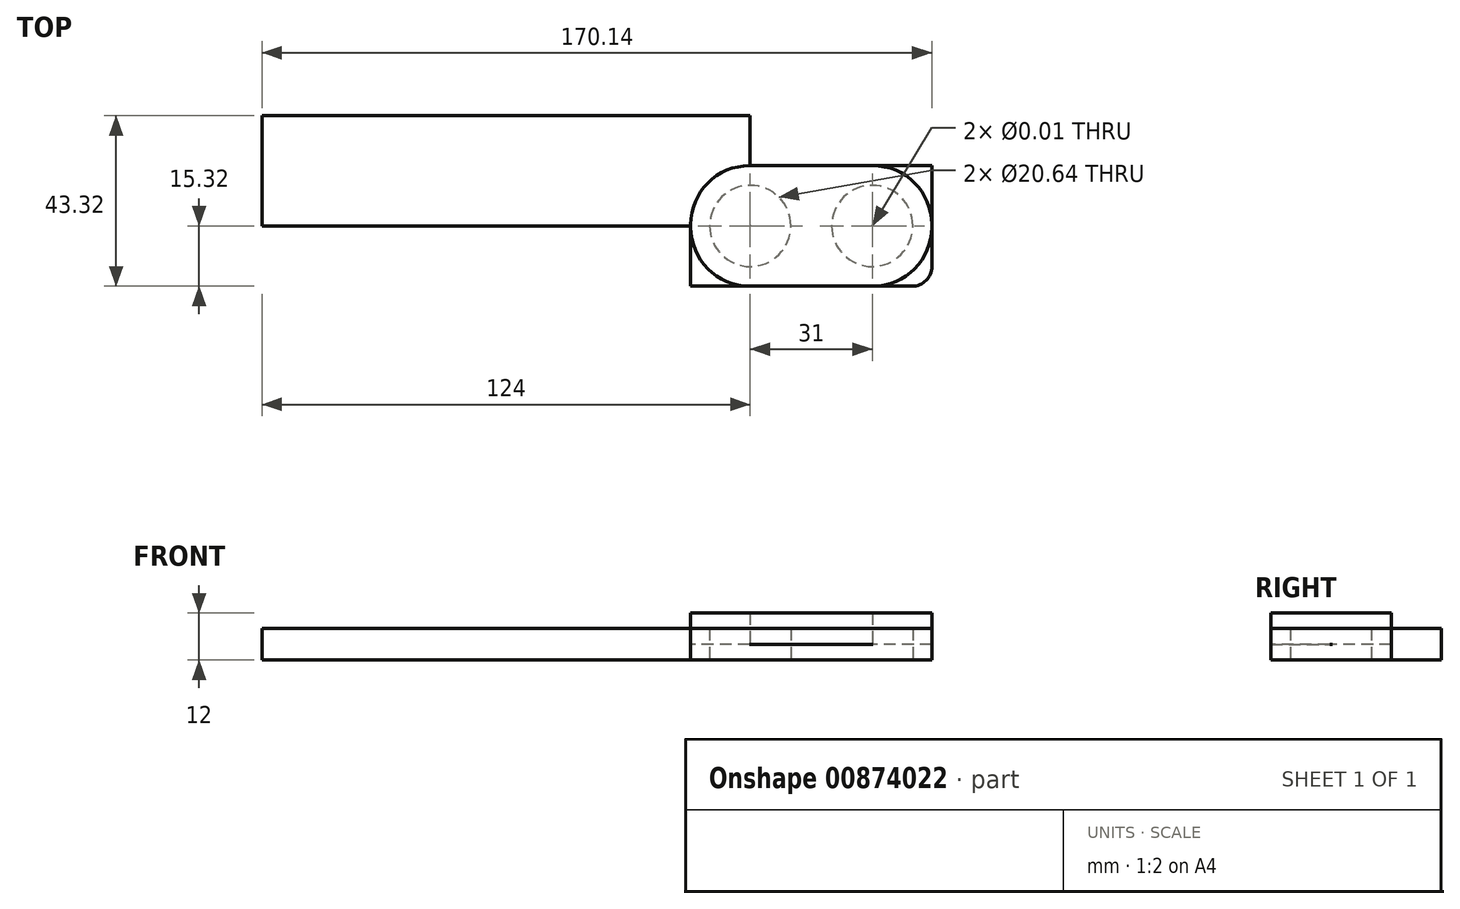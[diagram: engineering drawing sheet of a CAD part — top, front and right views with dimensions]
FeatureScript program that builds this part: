
annotation { "Feature Type Name" : "Feature", "Feature Type Description" : "" }
export const myFeature = defineFeature(function(context is Context, id is Id, definition is map)
    precondition{}
    {
        {
            var Q0;
            Q0=qCreatedBy(makeId("Top.planeOp"),FACE);
            var sketch = newSketch(context, id + "F0", { "sketchPlane" : qUnion([Q0])});
            skLineSegment(sketch, "E0.bottom", {"start": v(30.64, -15.32) * mm, "end": v(-30.64, -15.32) * mm});
            skLineSegment(sketch, "E0.top", {"start": v(30.64, 15.32) * mm, "end": v(-30.64, 15.32) * mm});
            skLineSegment(sketch, "E0.left", {"start": v(30.64, -15.32) * mm, "end": v(30.64, 15.32) * mm});
            skLineSegment(sketch, "E0.right", {"start": v(-30.64, -15.32) * mm, "end": v(-30.64, 15.32) * mm});
            skPoint(sketch, "E0.middle", {"position": v(0, 0) * mm});
            skPoint(sketch, "E1", {"position": v(0, -15.32) * mm});
            skLineSegment(sketch, "E2", {"start": v(0, -15.32) * mm, "end": v(0, 15.32) * mm});
            skCircle(sketch, "E3", {"center": v(15.5, 0) * mm, "radius": 10.32 * mm});
            skCircle(sketch, "E4", {"center": v(-15.5, 0) * mm, "radius": 10.32 * mm});
            skLineSegment(sketch, "E5.top", {"start": v(30.64, 28) * mm, "end": v(-30.64, 28) * mm});
            skLineSegment(sketch, "E5.left", {"start": v(30.64, 15.32) * mm, "end": v(30.64, 28) * mm});
            skLineSegment(sketch, "E5.right", {"start": v(-30.64, 15.32) * mm, "end": v(-30.64, 28) * mm});
            skLineSegment(sketch, "E6.bottom", {"start": v(-15.5, 0) * mm, "end": v(-139.5, 0) * mm});
            skLineSegment(sketch, "E6.top", {"start": v(-15.5, 28) * mm, "end": v(-139.5, 28) * mm});
            skLineSegment(sketch, "E6.left", {"start": v(-15.5, 0) * mm, "end": v(-15.5, 28) * mm});
            skLineSegment(sketch, "E6.right", {"start": v(-139.5, 0) * mm, "end": v(-139.5, 28) * mm});
            skPoint(sketch, "E7", {"position": v(-124.5, 14) * mm});
            skPoint(sketch, "E7.positionSnap0", {"position": v(-139.5, 14) * mm});
            skPoint(sketch, "E8", {"position": v(-65.5, 14) * mm});
            skPoint(sketch, "E9", {"position": v(-15.5, 14) * mm});
            skSolve(sketch);
        }
        {
            var Q0;
            {var subQ0=sQuery(id+"F0.wireOp",EDGE,"E0.right");Q0=makeQuery(id+"F0.imprint","IMPRINT",FACE,{"disambiguationData":[TD([[makeQuery(id+"F0.imprint","IMPRINT",EDGE,{"derivedFrom":subQ0}),-1.0]])]});}
            var Q1;
            {var subQ1=sQuery(id+"F0.wireOp",EDGE,"E0.left");Q1=makeQuery(id+"F0.imprint","IMPRINT",FACE,{"disambiguationData":[TD([[makeQuery(id+"F0.imprint","IMPRINT",EDGE,{"derivedFrom":subQ1}),1.0]])]});}
            var Q2;
            {var subQ0=sQuery(id+"F0.wireOp",EDGE,"E2");Q2=makeQuery(id+"F0.imprint","IMPRINT",FACE,{"disambiguationData":[TD([[makeQuery(id+"F0.imprint","IMPRINT",EDGE,{"derivedFrom":subQ0}),1.0]])]});}
            var Q3;
            {var subQ1=sQuery(id+"F0.wireOp",EDGE,"E5.top");Q3=makeQuery(id+"F0.imprint","IMPRINT",FACE,{"disambiguationData":[TD([[makeQuery(id+"F0.imprint","IMPRINT",EDGE,{"derivedFrom":subQ1}),1.0]])]});}
            var Q4;
            {var subQ0=sQuery(id+"F0.wireOp",EDGE,"E5.right");Q4=makeQuery(id+"F0.imprint","IMPRINT",FACE,{"disambiguationData":[TD([[makeQuery(id+"F0.imprint","IMPRINT",EDGE,{"derivedFrom":subQ0}),-1.0]])]});}
            var Q5;
            {var subQ5=sQuery(id+"F0.wireOp",EDGE,"E5.right");Q5=makeQuery(id+"F0.imprint","IMPRINT",FACE,{"disambiguationData":[TD([[makeQuery(id+"F0.imprint","IMPRINT",EDGE,{"derivedFrom":subQ5}),1.0]])]});}
            extrude(context, id + "F1", {"entities" : qUnion([Q0, Q1, Q2, Q3, Q4, Q5]), "endBound" : BoundingType.SYMMETRIC, "depth" : 8 * mm, "offsetDistance" : 25 * mm});
        }
        {
            var Q0;
            {var subQ0=sQuery(id+"F0.wireOp",EDGE,"E0.right");Q0=makeQuery(id+"F0.imprint","IMPRINT",FACE,{"disambiguationData":[TD([[makeQuery(id+"F0.imprint","IMPRINT",EDGE,{"derivedFrom":subQ0}),-1.0]])]});}
            var Q1;
            {var subQ0=sQuery(id+"F0.wireOp",EDGE,"E2");Q1=makeQuery(id+"F0.imprint","IMPRINT",FACE,{"disambiguationData":[TD([[makeQuery(id+"F0.imprint","IMPRINT",EDGE,{"derivedFrom":subQ0}),1.0]])]});}
            var Q2;
            {var subQ0=sQuery(id+"F0.wireOp",EDGE,"E0.left");Q2=makeQuery(id+"F0.imprint","IMPRINT",FACE,{"disambiguationData":[TD([[makeQuery(id+"F0.imprint","IMPRINT",EDGE,{"derivedFrom":subQ0}),1.0]])]});}
            var Q3;
            Q3=makeQuery(id+"F0.imprint","IMPRINT",FACE,{"disambiguationData":[TD([[makeQuery(id+"F0.imprint","IMPRINT",EDGE,{"derivedFrom":sQuery(id+"F0.wireOp",EDGE,"E3")}),1.0]])]});
            var Q4;
            {var subQ0=sQuery(id+"F0.wireOp",EDGE,"E6.bottom");var subQ1=sQuery(id+"F0.wireOp",EDGE,"E4");var subQ2=makeQuery(id+"F0.imprint","INTERSECT",VERTEX,{"derivedFrom":[subQ1,subQ0]});Q4=makeQuery(id+"F0.imprint","IMPRINT",FACE,{"disambiguationData":[TD([[makeQuery(id+"F0.imprint","IMPRINT",EDGE,{"disambiguationData":[TD([[subQ2,-1.0]])],"derivedFrom":subQ1}),1.0]])]});}
            var Q5;
            {var subQ0=sQuery(id+"F0.wireOp",EDGE,"E6.bottom");var subQ1=sQuery(id+"F0.wireOp",EDGE,"E4");var subQ2=makeQuery(id+"F0.imprint","INTERSECT",VERTEX,{"derivedFrom":[subQ1,subQ0]});Q5=makeQuery(id+"F0.imprint","IMPRINT",FACE,{"disambiguationData":[TD([[makeQuery(id+"F0.imprint","IMPRINT",EDGE,{"disambiguationData":[TD([[subQ2,1.0]])],"derivedFrom":subQ1}),1.0]])]});}
            extrude(context, id + "F2", {"entities" : qUnion([Q0, Q1, Q2, Q3, Q4, Q5]), "depth" : 8 * mm, "offsetDistance" : 25 * mm});
        }
        {
            var Q0;
            Q0=sQuery(id+"F0.wireOp",VERTEX,"E4.center");
            var Q1;
            Q1=sQuery(id+"F0.wireOp",VERTEX,"E3.center");
            var Q2;
            Q2=makeQuery(id+"F2.opExtrude","SWEPT_BODY",BODY,{"disambiguationData":[OSD([sQuery(id+"F0.wireOp",EDGE,"E0.bottom"),sQuery(id+"F0.wireOp",EDGE,"E0.top"),sQuery(id+"F0.wireOp",EDGE,"E0.left"),sQuery(id+"F0.wireOp",EDGE,"E0.right")])]});
            hole(context, id + "F3", {"style" : HoleStyle.SIMPLE, "endStyle" : HoleEndStyle.THROUGH, "oppositeDirection" : true, "standardTappedOrClearance" : lookupTablePath({ "standard" : "ANSI", "size" : "3/8 (0.38)", "type" : "Drilled" }), "standardBlindInLast" : lookupTablePath({ "standard" : "ANSI", "size" : "3/8", "type" : "Drilled" }), "holeDiameter" : 3 / 203.2 * mm, "majorDiameter" : 5 * mm, "isTappedThrough" : true, "tappedDepth" : 12 * mm, "tapClearance" : 3, "locations" : qUnion([Q0, Q1]), "scope" : qUnion([Q2])});
        }
        {
            var Q0;
            Q0=makeQuery(id+"F2.opExtrude","SWEPT_EDGE",EDGE,{"disambiguationData":[OSD([sQuery(id+"F0.wireOp",EDGE,"E0.top"),sQuery(id+"F0.wireOp",EDGE,"E0.left")])]});
            var Q1;
            Q1=makeQuery(id+"F2.opExtrude","SWEPT_EDGE",EDGE,{"disambiguationData":[OSD([sQuery(id+"F0.wireOp",EDGE,"E0.bottom"),sQuery(id+"F0.wireOp",EDGE,"E0.left")])]});
            var Q2;
            Q2=makeQuery(id+"F2.opExtrude","SWEPT_EDGE",EDGE,{"disambiguationData":[OSD([sQuery(id+"F0.wireOp",EDGE,"E0.bottom"),sQuery(id+"F0.wireOp",EDGE,"E0.right")])]});
            var Q3;
            Q3=makeQuery(id+"F2.opExtrude","SWEPT_EDGE",EDGE,{"disambiguationData":[OSD([sQuery(id+"F0.wireOp",EDGE,"E0.top"),sQuery(id+"F0.wireOp",EDGE,"E0.right")])]});
            var Q4;
            Q4=makeQuery(id+"F2.opExtrude","SWEPT_EDGE",EDGE,{"disambiguationData":[OSD([sQuery(id+"F0.wireOp",EDGE,"E0.left"),sQuery(id+"F0.wireOp",EDGE,"E0.top"),sQuery(id+"F0.wireOp",EDGE,"E5.left")])]});
            var Q5;
            Q5=makeQuery(id+"F2.opExtrude","SWEPT_EDGE",EDGE,{"disambiguationData":[OSD([sQuery(id+"F0.wireOp",EDGE,"E0.right"),sQuery(id+"F0.wireOp",EDGE,"E0.top"),sQuery(id+"F0.wireOp",EDGE,"E5.right")])]});
            fillet(context, id + "F4", {"entities" : qUnion([Q0, Q1, Q2, Q3, Q4, Q5]), "radius" : 15 * mm, "tangentPropagation" : true, "allowEdgeOverflow" : false});
        }
        {
            var Q0;
            Q0=makeQuery(id+"F1.opExtrude","SWEPT_EDGE",EDGE,{"disambiguationData":[OSD([sQuery(id+"F0.wireOp",EDGE,"E0.bottom"),sQuery(id+"F0.wireOp",EDGE,"E0.left")])]});
            fillet(context, id + "F5", {"entities" : qUnion([Q0]), "radius" : 5 * mm, "tangentPropagation" : true, "allowEdgeOverflow" : false});
        }
    });
